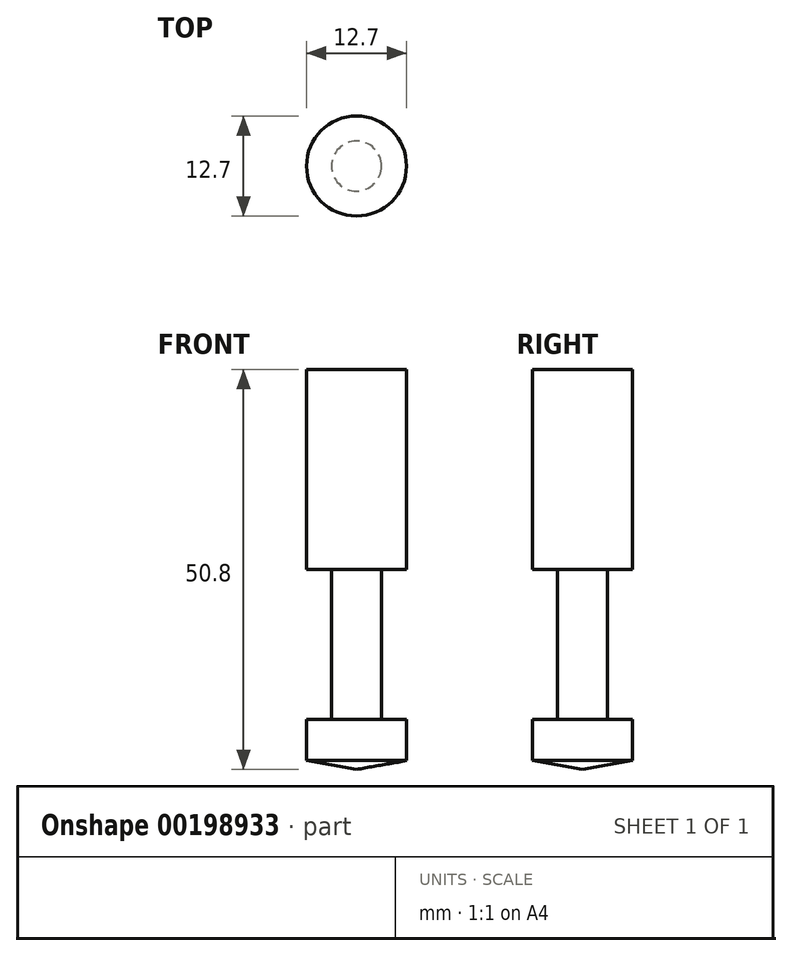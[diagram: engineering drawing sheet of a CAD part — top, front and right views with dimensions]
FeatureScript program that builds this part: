
annotation { "Feature Type Name" : "Feature", "Feature Type Description" : "" }
export const myFeature = defineFeature(function(context is Context, id is Id, definition is map)
    precondition{}
    {
        {
            var Q0;
            Q0=qCreatedBy(makeId("Top.planeOp"),FACE);
            var sketch = newSketch(context, id + "F0", { "sketchPlane" : qUnion([Q0])});
            skCircle(sketch, "E0", {"center": v(0, 0) * mm, "radius": 6.35 * mm});
            skSolve(sketch);
        }
        {
            var Q0;
            Q0 = qSketchRegion(id + "F0", true);
            extrude(context, id + "F1", {"entities" : qUnion([Q0]), "depth" : 6.35 * mm});
        }
        {
            var Q0;
            Q0=makeQuery(id+"F1.opExtrude","CAP_FACE",FACE,{"disambiguationData":[OSD([sQuery(id+"F0.wireOp",EDGE,"E0")])],"isStart":false});
            var sketch = newSketch(context, id + "F2", { "sketchPlane" : qUnion([Q0])});
            skCircle(sketch, "E1", {"center": v(0, 0) * mm, "radius": 3.18 * mm});
            skSolve(sketch);
        }
        {
            var Q0;
            Q0=makeQuery(id+"F2.imprint","IMPRINT",FACE,{"disambiguationData":[TD([[makeQuery(id+"F2.imprint","IMPRINT",EDGE,{"derivedFrom":sQuery(id+"F2.wireOp",EDGE,"E1")}),1.0]])]});
            extrude(context, id + "F3", {"entities" : qUnion([Q0]), "operationType" : NewBodyOperationType.ADD, "depth" : 19.05 * mm});
        }
        {
            var Q0;
            Q0=makeQuery(id+"F3.opExtrude","CAP_FACE",FACE,{"disambiguationData":[OSD([sQuery(id+"F2.wireOp",EDGE,"E1")])],"isStart":false});
            var sketch = newSketch(context, id + "F4", { "sketchPlane" : qUnion([Q0])});
            skCircle(sketch, "E2", {"center": v(0, 0) * mm, "radius": 6.35 * mm});
            skSolve(sketch);
        }
        {
            var Q0;
            Q0 = qSketchRegion(id + "F4", true);
            extrude(context, id + "F5", {"entities" : qUnion([Q0]), "operationType" : NewBodyOperationType.ADD, "depth" : 25.4 * mm});
        }
        {
            var Q0;
            Q0=makeQuery(id+"F1.opExtrude","CAP_EDGE",EDGE,{"disambiguationData":[OSD([sQuery(id+"F0.wireOp",EDGE,"E0")])],"isStart":true});
            chamfer(context, id + "F6", {"entities" : qUnion([Q0]), "chamferType" : ChamferType.OFFSET_ANGLE, "width" : 6.35 * mm, "oppositeDirection" : true, "angle" : 10 * degree, "tangentPropagation" : true});
        }
    });
